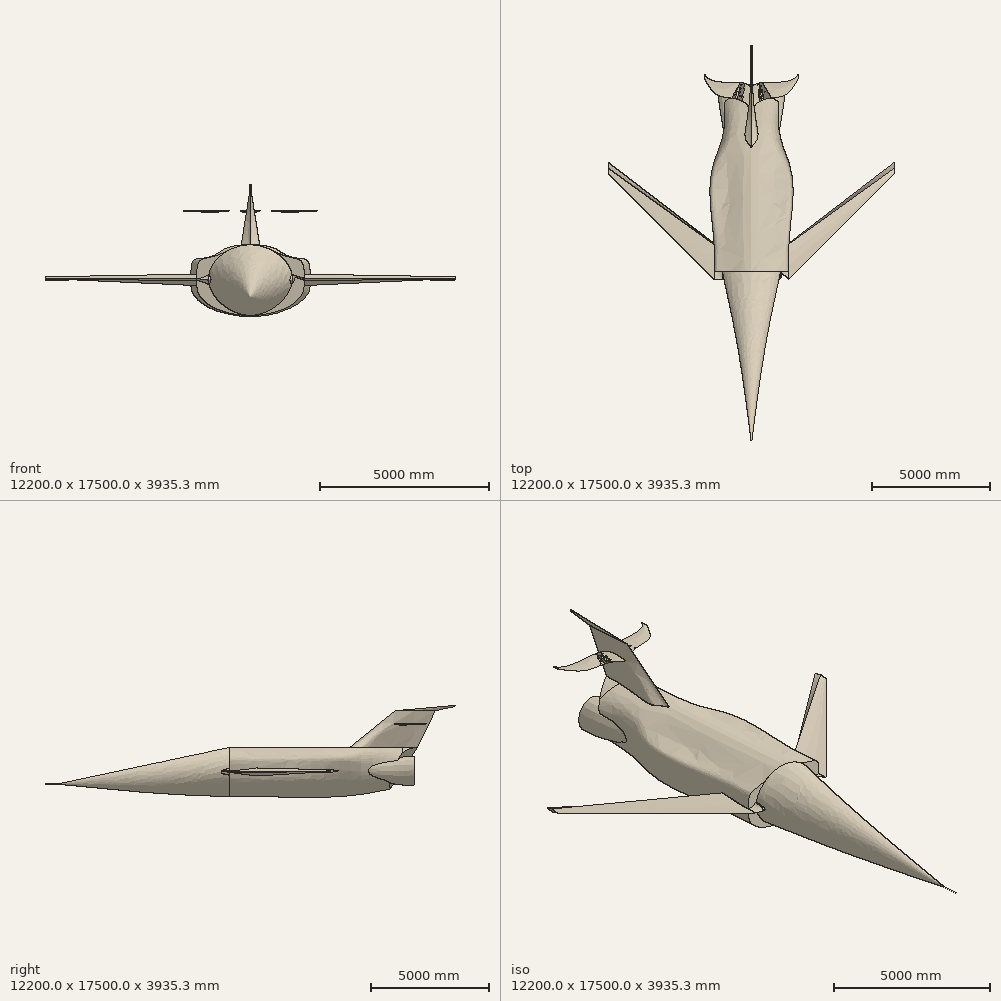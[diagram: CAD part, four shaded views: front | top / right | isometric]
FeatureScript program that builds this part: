
annotation { "Feature Type Name" : "Feature", "Feature Type Description" : "" }
export const myFeature = defineFeature(function(context is Context, id is Id, definition is map)
    precondition{}
    {
        {
            var Q0;
            Q0=qCreatedBy(makeId("Right.planeOp"),FACE);
            var sketch = newSketch(context, id + "F0", { "sketchPlane" : qUnion([Q0])});
            skLineSegment(sketch, "E0", {"start": v(0, 0) * mm, "end": v(-1750, 0) * mm});
            skLineSegment(sketch, "E1", {"start": v(-1750, 0) * mm, "end": v(-3500, 0) * mm});
            skLineSegment(sketch, "E2", {"start": v(-3500, 0) * mm, "end": v(-3500, -1000) * mm});
            skLineSegment(sketch, "E3", {"start": v(-3500, -1000) * mm, "end": v(-8500, -1000) * mm});
            skLineSegment(sketch, "E4", {"start": v(-8500, -1000) * mm, "end": v(-8500, -562.6) * mm});
            skLineSegment(sketch, "E5", {"start": v(-1164.59, 0) * mm, "end": v(-1164.59, 1000) * mm});
            skLineSegment(sketch, "E6", {"start": v(-1164.59, 1000) * mm, "end": v(-8500, -562.6) * mm});
            skLineSegment(sketch, "E7", {"start": v(-8500, -562.6) * mm, "end": v(-3500, -1000) * mm});
            skLineSegment(sketch, "E8", {"start": v(-3500, 0) * mm, "end": v(-3500, 502.5) * mm});
            skLineSegment(sketch, "E9", {"start": v(-8500, -562.6) * mm, "end": v(-8450, -562.6) * mm});
            skLineSegment(sketch, "E10", {"start": v(-8450, -562.6) * mm, "end": v(-8450, -551.95) * mm});
            skLineSegment(sketch, "E11", {"start": v(-8450, -562.6) * mm, "end": v(-8450, -566.97) * mm});
            skSolve(sketch);
        }
        {
            var Q0;
            Q0=sQuery(id+"F0.wireOp",EDGE,"E5");
            cPlane(context, id + "F1", {"entities" : qUnion([Q0]), "cplaneType" : CPlaneType.LINE_ANGLE, "offset" : 25 * mm, "angle" : 90 * degree, "oppositeDirection" : true, "width" : 150 * mm, "height" : 150 * mm});
        }
        {
            var Q0;
            Q0=qCreatedBy(id+"F1.planeOp",FACE);
            var sketch = newSketch(context, id + "F2", { "sketchPlane" : qUnion([Q0])});
            skPoint(sketch, "E12.middle", {"position": v(0, 0) * mm});
            skFitSpline(sketch, "E13", {"points": [v(0, 1000) * mm, v(-1060, 662.5) * mm, v(-1517.6, 506.84) * mm, v(-1600, 0) * mm, v(-1517.6, -506.84) * mm, v(-750, -1000) * mm, v(750, -1000) * mm, v(1517.6, -506.84) * mm, v(1600, 0) * mm, v(1517.6, 506.84) * mm, v(1060, 662.5) * mm, v(0, 1000) * mm]});
            skSolve(sketch);
        }
        {
            var Q0;
            Q0=qCreatedBy(makeId("Front.planeOp"),FACE);
            var sketch = newSketch(context, id + "F3", { "sketchPlane" : qUnion([Q0])});
            skPoint(sketch, "E14.middle", {"position": v(0, 0) * mm});
            skFitSpline(sketch, "E15", {"points": [v(0, 1000) * mm, v(-1060, 662.5) * mm, v(-1517.6, 506.84) * mm, v(-1600, 0) * mm, v(-1517.6, -506.84) * mm, v(-750, -1000) * mm, v(750, -1000) * mm, v(1517.6, -506.84) * mm, v(1600, 0) * mm, v(1517.6, 506.84) * mm, v(1060, 662.5) * mm, v(0, 1000) * mm]});
            skSolve(sketch);
        }
        {
            var Q0;
            Q0=qCreatedBy(makeId("Front.planeOp"),FACE);
            cPlane(context, id + "F4", {"entities" : qUnion([Q0]), "cplaneType" : CPlaneType.OFFSET, "offset" : 3500 * mm, "oppositeDirection" : true, "width" : 150 * mm, "height" : 150 * mm});
        }
        {
            var Q0;
            Q0=qCreatedBy(id+"F4.planeOp",FACE);
            var sketch = newSketch(context, id + "F5", { "sketchPlane" : qUnion([Q0])});
            skPoint(sketch, "E16.middle", {"position": v(0, 0) * mm});
            skFitSpline(sketch, "E17", {"points": [v(0, 1000) * mm, v(-1060, 662.5) * mm, v(-1517.6, 506.84) * mm, v(-1600, 0) * mm, v(-1517.6, -506.84) * mm, v(-750, -1000) * mm, v(750, -1000) * mm, v(1517.6, -506.84) * mm, v(1600, 0) * mm, v(1517.6, 506.84) * mm, v(1060, 662.5) * mm, v(0, 1000) * mm]});
            skSolve(sketch);
        }
        {
            var Q0;
            Q0=qCreatedBy(makeId("Front.planeOp"),FACE);
            cPlane(context, id + "F6", {"entities" : qUnion([Q0]), "cplaneType" : CPlaneType.OFFSET, "offset" : 4500 * mm, "oppositeDirection" : true, "width" : 150 * mm, "height" : 150 * mm});
        }
        {
            var Q0;
            Q0=qCreatedBy(id+"F6.planeOp",FACE);
            var sketch = newSketch(context, id + "F7", { "sketchPlane" : qUnion([Q0])});
            skPoint(sketch, "E18.middle", {"position": v(0, 0) * mm});
            skFitSpline(sketch, "E19", {"points": [v(0, 1000) * mm, v(-1060, 662.5) * mm, v(-1250, 0) * mm, v(-1060, -662.5) * mm, v(0, -1000) * mm, v(1060, -662.5) * mm, v(1250, 0) * mm, v(1060, 662.5) * mm, v(0, 1000) * mm]});
            skSolve(sketch);
        }
        {
            var Q0;
            Q0=qCreatedBy(makeId("Front.planeOp"),FACE);
            cPlane(context, id + "F8", {"entities" : qUnion([Q0]), "cplaneType" : CPlaneType.OFFSET, "offset" : 6232.05 * mm, "oppositeDirection" : true, "width" : 150 * mm, "height" : 150 * mm});
        }
        {
            var Q0;
            Q0=qCreatedBy(id+"F8.planeOp",FACE);
            var sketch = newSketch(context, id + "F9", { "sketchPlane" : qUnion([Q0])});
            skPoint(sketch, "E20.middle", {"position": v(0, 0) * mm});
            skFitSpline(sketch, "E21", {"points": [v(0, 1000) * mm, v(-1060, 662.5) * mm, v(-1250, 0) * mm, v(-848, -530) * mm, v(848, -530) * mm, v(1250, 0) * mm, v(1060, 662.5) * mm, v(0, 1000) * mm]});
            skSolve(sketch);
        }
        {
            var Q0;
            Q0=makeQuery(id+"F2.imprint","IMPRINT",FACE,{"disambiguationData":[TD([[makeQuery(id+"F2.imprint","IMPRINT",EDGE,{"derivedFrom":sQuery(id+"F2.wireOp",EDGE,"E13")}),1.0]])]});
            var Q1;
            Q1=makeQuery(id+"F3.imprint","IMPRINT",FACE,{"disambiguationData":[TD([[makeQuery(id+"F3.imprint","IMPRINT",EDGE,{"derivedFrom":sQuery(id+"F3.wireOp",EDGE,"E15")}),1.0]])]});
            var Q2;
            Q2=makeQuery(id+"F5.imprint","IMPRINT",FACE,{"disambiguationData":[TD([[makeQuery(id+"F5.imprint","IMPRINT",EDGE,{"derivedFrom":sQuery(id+"F5.wireOp",EDGE,"E17")}),1.0]])]});
            var Q3;
            Q3=makeQuery(id+"F7.imprint","IMPRINT",FACE,{"disambiguationData":[TD([[makeQuery(id+"F7.imprint","IMPRINT",EDGE,{"derivedFrom":sQuery(id+"F7.wireOp",EDGE,"E19")}),1.0]])]});
            var Q4;
            Q4=makeQuery(id+"F9.imprint","IMPRINT",FACE,{"disambiguationData":[TD([[makeQuery(id+"F9.imprint","IMPRINT",EDGE,{"derivedFrom":sQuery(id+"F9.wireOp",EDGE,"E21")}),1.0]])]});
            loft(context, id + "F10", {"sheetProfilesArray" : [{ "sheetProfileEntities" : qUnion([Q0]) }, { "sheetProfileEntities" : qUnion([Q1]) }, { "sheetProfileEntities" : qUnion([Q2]) }, { "sheetProfileEntities" : qUnion([Q3]) }, { "sheetProfileEntities" : qUnion([Q4]) }]});
        }
        {
            var Q0;
            Q0=makeQuery(id+"F10.opLoft","CAP_FACE",FACE,{"disambiguationData":[OSD([makeQuery(id+"F9.imprint","IMPRINT",FACE,{"disambiguationData":[TD([[makeQuery(id+"F9.imprint","IMPRINT",EDGE,{"derivedFrom":sQuery(id+"F9.wireOp",EDGE,"E21")}),1.0]])]})])],"isStart":true});
            extrude(context, id + "F11", {"entities" : qUnion([Q0]), "operationType" : NewBodyOperationType.ADD, "depth" : 649.4 * mm, "offsetDistance" : 25 * mm});
        }
        {
            var Q0;
            Q0=qCreatedBy(makeId("Right.planeOp"),FACE);
            var sketch = newSketch(context, id + "F12", { "sketchPlane" : qUnion([Q0])});
            skLineSegment(sketch, "E22", {"start": v(0, 0) * mm, "end": v(4500, 0) * mm});
            skLineSegment(sketch, "E23", {"start": v(4500, 0) * mm, "end": v(6232.05, 0) * mm});
            skLineSegment(sketch, "E24", {"start": v(4500, 0) * mm, "end": v(4500, 1000) * mm});
            skLineSegment(sketch, "E25", {"start": v(4500, 1000) * mm, "end": v(6881.46, 1000) * mm});
            skLineSegment(sketch, "E26", {"start": v(6881.46, 1000) * mm, "end": v(6881.46, -1000) * mm});
            skLineSegment(sketch, "E27", {"start": v(6881.46, 1000) * mm, "end": v(6232.05, 0) * mm});
            skLineSegment(sketch, "E28", {"start": v(6232.05, 0) * mm, "end": v(5582.64, -1000) * mm});
            skLineSegment(sketch, "E29", {"start": v(5582.64, -1000) * mm, "end": v(6881.46, -1000) * mm});
            skSolve(sketch);
        }
        {
            var Q0;
            Q0=makeQuery(id+"F12.imprint","IMPRINT",FACE,{"disambiguationData":[TD([[makeQuery(id+"F12.imprint","IMPRINT",EDGE,{"derivedFrom":sQuery(id+"F12.wireOp",EDGE,"E26")}),-1.0]])]});
            var Q1;
            Q1=sQuery(id+"F12.wireOp",EDGE,"E25");
            revolve(context, id + "F13", {"operationType" : NewBodyOperationType.REMOVE, "entities" : qUnion([Q0]), "axis" : qUnion([Q1]), "revolveType" : RevolveType.SYMMETRIC, "oppositeDirection" : true, "angle" : 182 * degree});
        }
        {
            var Q0;
            Q0=qCreatedBy(id+"F1.planeOp",FACE);
            var sketch = newSketch(context, id + "F14", { "sketchPlane" : qUnion([Q0])});
            skFitSpline(sketch, "E30", {"points": [v(0, 1000) * mm, v(-1250, 0) * mm, v(0, -1099.92) * mm, v(1250, 0) * mm, v(0, 1000) * mm]});
            skSolve(sketch);
        }
        {
            var Q0;
            Q0=qCreatedBy(makeId("Front.planeOp"),FACE);
            cPlane(context, id + "F15", {"entities" : qUnion([Q0]), "cplaneType" : CPlaneType.OFFSET, "offset" : 3500 * mm, "width" : 150 * mm, "height" : 150 * mm});
        }
        {
            var Q0;
            Q0=qCreatedBy(id+"F15.planeOp",FACE);
            var sketch = newSketch(context, id + "F16", { "sketchPlane" : qUnion([Q0])});
            skCircle(sketch, "E31", {"center": v(0, -248.75) * mm, "radius": 751.25 * mm});
            skSolve(sketch);
        }
        {
            var Q0;
            Q0=qCreatedBy(makeId("Front.planeOp"),FACE);
            cPlane(context, id + "F17", {"entities" : qUnion([Q0]), "cplaneType" : CPlaneType.OFFSET, "offset" : 8450 * mm, "width" : 150 * mm, "height" : 150 * mm});
        }
        {
            var Q0;
            Q0=qCreatedBy(id+"F17.planeOp",FACE);
            var sketch = newSketch(context, id + "F18", { "sketchPlane" : qUnion([Q0])});
            skCircle(sketch, "E32", {"center": v(0, -559.46) * mm, "radius": 7.51 * mm});
            skSolve(sketch);
        }
        {
            var Q1;
            Q1=makeQuery(id+"F18.imprint","IMPRINT",FACE,{"disambiguationData":[TD([[makeQuery(id+"F18.imprint","IMPRINT",EDGE,{"derivedFrom":sQuery(id+"F18.wireOp",EDGE,"E32")}),1.0]])]});
            var Q2;
            Q2=makeQuery(id+"F16.imprint","IMPRINT",FACE,{"disambiguationData":[TD([[makeQuery(id+"F16.imprint","IMPRINT",EDGE,{"derivedFrom":sQuery(id+"F16.wireOp",EDGE,"E31")}),1.0]])]});
            var Q3;
            Q3=makeQuery(id+"F14.imprint","IMPRINT",FACE,{"disambiguationData":[TD([[makeQuery(id+"F14.imprint","IMPRINT",EDGE,{"derivedFrom":sQuery(id+"F14.wireOp",EDGE,"E30")}),1.0]])]});
            loft(context, id + "F19", {"operationType" : NewBodyOperationType.ADD, "sheetProfilesArray" : [{ "sheetProfileEntities" : qUnion([Q1]) }, { "sheetProfileEntities" : qUnion([Q2]) }, { "sheetProfileEntities" : qUnion([Q3]) }]});
        }
        {
            var Q0;
            Q0=makeQuery(id+"F19.opLoft","CAP_FACE",FACE,{"disambiguationData":[OSD([makeQuery(id+"F18.imprint","IMPRINT",FACE,{"disambiguationData":[TD([[makeQuery(id+"F18.imprint","IMPRINT",EDGE,{"derivedFrom":sQuery(id+"F18.wireOp",EDGE,"E32")}),1.0]])]})])],"isStart":true});
            extrude(context, id + "F20", {"entities" : qUnion([Q0]), "operationType" : NewBodyOperationType.ADD, "depth" : 550 * mm, "offsetDistance" : 25 * mm});
        }
        {
            var Q0;
            Q0=qCreatedBy(makeId("Front.planeOp"),FACE);
            cPlane(context, id + "F21", {"entities" : qUnion([Q0]), "cplaneType" : CPlaneType.OFFSET, "offset" : 3500 * mm, "oppositeDirection" : true, "width" : 150 * mm, "height" : 150 * mm});
        }
        {
            var Q0;
            Q0=qCreatedBy(id+"F21.planeOp",FACE);
            var sketch = newSketch(context, id + "F22", { "sketchPlane" : qUnion([Q0])});
            skCircle(sketch, "E33", {"center": v(-800, 0) * mm, "radius": 600 * mm});
            skCircle(sketch, "E34", {"center": v(800, 0) * mm, "radius": 600 * mm});
            skSolve(sketch);
        }
        {
            var Q0;
            Q0=qCreatedBy(makeId("Front.planeOp"),FACE);
            cPlane(context, id + "F23", {"entities" : qUnion([Q0]), "cplaneType" : CPlaneType.OFFSET, "offset" : 4500 * mm, "oppositeDirection" : true, "width" : 150 * mm, "height" : 150 * mm});
        }
        {
            var Q0;
            Q0=qCreatedBy(id+"F23.planeOp",FACE);
            var sketch = newSketch(context, id + "F24", { "sketchPlane" : qUnion([Q0])});
            skCircle(sketch, "E35", {"center": v(-800, 0) * mm, "radius": 400 * mm});
            skCircle(sketch, "E36", {"center": v(800, 0) * mm, "radius": 400 * mm});
            skSolve(sketch);
        }
        {
            var Q0;
            Q0=qCreatedBy(makeId("Front.planeOp"),FACE);
            cPlane(context, id + "F25", {"entities" : qUnion([Q0]), "cplaneType" : CPlaneType.OFFSET, "offset" : 6232.05 * mm, "oppositeDirection" : true, "width" : 150 * mm, "height" : 150 * mm});
        }
        {
            var Q0;
            Q0=qCreatedBy(id+"F25.planeOp",FACE);
            var sketch = newSketch(context, id + "F26", { "sketchPlane" : qUnion([Q0])});
            skCircle(sketch, "E37", {"center": v(-800, 0) * mm, "radius": 600 * mm});
            skCircle(sketch, "E38", {"center": v(800, 0) * mm, "radius": 600 * mm});
            skSolve(sketch);
        }
        {
            var Q0;
            Q0=qCreatedBy(makeId("Front.planeOp"),FACE);
            cPlane(context, id + "F27", {"entities" : qUnion([Q0]), "cplaneType" : CPlaneType.OFFSET, "offset" : 6732.05 * mm, "oppositeDirection" : true, "width" : 150 * mm, "height" : 150 * mm});
        }
        {
            var Q0;
            Q0=qCreatedBy(id+"F27.planeOp",FACE);
            var sketch = newSketch(context, id + "F28", { "sketchPlane" : qUnion([Q0])});
            skCircle(sketch, "E39", {"center": v(-800, 0) * mm, "radius": 600 * mm});
            skCircle(sketch, "E40", {"center": v(800, 0) * mm, "radius": 600 * mm});
            skSolve(sketch);
        }
        {
            var Q0;
            Q0=makeQuery(id+"F22.imprint","IMPRINT",FACE,{"disambiguationData":[TD([[makeQuery(id+"F22.imprint","IMPRINT",EDGE,{"derivedFrom":sQuery(id+"F22.wireOp",EDGE,"E33")}),1.0]])]});
            var Q1;
            Q1=makeQuery(id+"F24.imprint","IMPRINT",FACE,{"disambiguationData":[TD([[makeQuery(id+"F24.imprint","IMPRINT",EDGE,{"derivedFrom":sQuery(id+"F24.wireOp",EDGE,"E35")}),1.0]])]});
            var Q2;
            Q2=makeQuery(id+"F26.imprint","IMPRINT",FACE,{"disambiguationData":[TD([[makeQuery(id+"F26.imprint","IMPRINT",EDGE,{"derivedFrom":sQuery(id+"F26.wireOp",EDGE,"E37")}),1.0]])]});
            var Q3;
            Q3=makeQuery(id+"F28.imprint","IMPRINT",FACE,{"disambiguationData":[TD([[makeQuery(id+"F28.imprint","IMPRINT",EDGE,{"derivedFrom":sQuery(id+"F28.wireOp",EDGE,"E39")}),1.0]])]});
            loft(context, id + "F29", {"sheetProfilesArray" : [{ "sheetProfileEntities" : qUnion([Q0]) }, { "sheetProfileEntities" : qUnion([Q1]) }, { "sheetProfileEntities" : qUnion([Q2]) }, { "sheetProfileEntities" : qUnion([Q3]) }]});
        }
        {
            var Q0;
            Q0=makeQuery(id+"F22.imprint","IMPRINT",FACE,{"disambiguationData":[TD([[makeQuery(id+"F22.imprint","IMPRINT",EDGE,{"derivedFrom":sQuery(id+"F22.wireOp",EDGE,"E34")}),1.0]])]});
            var Q1;
            Q1=makeQuery(id+"F24.imprint","IMPRINT",FACE,{"disambiguationData":[TD([[makeQuery(id+"F24.imprint","IMPRINT",EDGE,{"derivedFrom":sQuery(id+"F24.wireOp",EDGE,"E36")}),1.0]])]});
            var Q2;
            Q2=makeQuery(id+"F26.imprint","IMPRINT",FACE,{"disambiguationData":[TD([[makeQuery(id+"F26.imprint","IMPRINT",EDGE,{"derivedFrom":sQuery(id+"F26.wireOp",EDGE,"E38")}),1.0]])]});
            var Q3;
            Q3=makeQuery(id+"F28.imprint","IMPRINT",FACE,{"disambiguationData":[TD([[makeQuery(id+"F28.imprint","IMPRINT",EDGE,{"derivedFrom":sQuery(id+"F28.wireOp",EDGE,"E40")}),1.0]])]});
            loft(context, id + "F30", {"sheetProfilesArray" : [{ "sheetProfileEntities" : qUnion([Q0]) }, { "sheetProfileEntities" : qUnion([Q1]) }, { "sheetProfileEntities" : qUnion([Q2]) }, { "sheetProfileEntities" : qUnion([Q3]) }]});
        }
        {
            var Q0;
            Q0=qCreatedBy(makeId("Right.planeOp"),FACE);
            var sketch = newSketch(context, id + "F31", { "sketchPlane" : qUnion([Q0])});
            skFitSpline(sketch, "E41", {"points": [v(-1500, -50) * mm, v(0, 250) * mm, v(3000, -50) * mm, v(0, -250) * mm, v(-1500, -50) * mm]});
            skSolve(sketch);
        }
        {
            var Q0;
            Q0=qCreatedBy(makeId("Right.planeOp"),FACE);
            cPlane(context, id + "F32", {"entities" : qUnion([Q0]), "cplaneType" : CPlaneType.OFFSET, "offset" : 1600 * mm, "oppositeDirection" : true, "width" : 150 * mm, "height" : 150 * mm});
        }
        {
            var Q0;
            Q0=qCreatedBy(id+"F32.planeOp",FACE);
            var sketch = newSketch(context, id + "F33", { "sketchPlane" : qUnion([Q0])});
            skFitSpline(sketch, "E42", {"points": [v(-1500, 0) * mm, v(1000, 250) * mm, v(3500, 0) * mm], "startDerivative": vector(7500, 0) * mm, "endDerivative": vector(7500, 0) * mm});
            skFitSpline(sketch, "E43", {"points": [v(-1500, 0) * mm, v(1000, -250) * mm, v(3500, 0) * mm], "startDerivative": vector(5000, -750) * mm, "endDerivative": vector(7500, 0) * mm});
            skSolve(sketch);
        }
        {
            var Q0;
            Q0=qCreatedBy(makeId("Right.planeOp"),FACE);
            cPlane(context, id + "F34", {"entities" : qUnion([Q0]), "cplaneType" : CPlaneType.OFFSET, "offset" : 1600 * mm, "width" : 150 * mm, "height" : 150 * mm});
        }
        {
            var Q0;
            Q0=qCreatedBy(id+"F34.planeOp",FACE);
            var sketch = newSketch(context, id + "F35", { "sketchPlane" : qUnion([Q0])});
            skFitSpline(sketch, "E44", {"points": [v(-1500, 0) * mm, v(1000, 250) * mm, v(3500, 0) * mm], "startDerivative": vector(7500, 0) * mm, "endDerivative": vector(7500, 0) * mm});
            skFitSpline(sketch, "E45", {"points": [v(-1500, 0) * mm, v(1000, -250) * mm, v(3500, 0) * mm], "startDerivative": vector(5000, -750) * mm, "endDerivative": vector(7500, 0) * mm});
            skSolve(sketch);
        }
        {
            var Q0;
            Q0=qCreatedBy(makeId("Right.planeOp"),FACE);
            cPlane(context, id + "F36", {"entities" : qUnion([Q0]), "cplaneType" : CPlaneType.OFFSET, "offset" : 6100 * mm, "oppositeDirection" : true, "width" : 150 * mm, "height" : 150 * mm});
        }
        {
            var Q0;
            Q0=qCreatedBy(id+"F36.planeOp",FACE);
            var sketch = newSketch(context, id + "F37", { "sketchPlane" : qUnion([Q0])});
            skFitSpline(sketch, "E46", {"points": [v(3000, 0) * mm, v(3250, 50) * mm, v(3500, 0) * mm], "startDerivative": vector(750, 0) * mm, "endDerivative": vector(750, 0) * mm});
            skFitSpline(sketch, "E47", {"points": [v(3000, 0) * mm, v(3250, -50) * mm, v(3500, 0) * mm], "startDerivative": vector(500, -150) * mm, "endDerivative": vector(750, 0) * mm});
            skSolve(sketch);
        }
        {
            var Q0;
            Q0=qCreatedBy(makeId("Right.planeOp"),FACE);
            cPlane(context, id + "F38", {"entities" : qUnion([Q0]), "cplaneType" : CPlaneType.OFFSET, "offset" : 6100 * mm, "width" : 150 * mm, "height" : 150 * mm});
        }
        {
            var Q0;
            Q0=qCreatedBy(id+"F38.planeOp",FACE);
            var sketch = newSketch(context, id + "F39", { "sketchPlane" : qUnion([Q0])});
            skFitSpline(sketch, "E48", {"points": [v(3000, 0) * mm, v(3250, 50) * mm, v(3500, 0) * mm], "startDerivative": vector(750, 0) * mm, "endDerivative": vector(750, 0) * mm});
            skFitSpline(sketch, "E49", {"points": [v(3000, 0) * mm, v(3250, -50) * mm, v(3500, 0) * mm], "startDerivative": vector(500, -150) * mm, "endDerivative": vector(750, 0) * mm});
            skSolve(sketch);
        }
        {
            var Q0;
            Q0=qSketchRegion(id+"F31",true);
            extrude(context, id + "F40", {"entities" : qUnion([Q0]), "endBound" : BoundingType.SYMMETRIC, "depth" : 2500 * mm, "offsetDistance" : 25 * mm});
        }
        {
            var Q1;
            Q1=makeQuery(id+"F40.opExtrude","CAP_FACE",FACE,{"disambiguationData":[OSD([sQuery(id+"F31.wireOp",EDGE,"E41")])],"isStart":true});
            var Q2;
            {var subQ0=sQuery(id+"F33.wireOp",EDGE,"E42");Q2=makeQuery(id+"F33.imprint","IMPRINT",FACE,{"disambiguationData":[TD([[makeQuery(id+"F33.imprint","IMPRINT",EDGE,{"derivedFrom":subQ0}),-1.0]])]});}
            loft(context, id + "F41", {"operationType" : NewBodyOperationType.ADD, "sheetProfilesArray" : [{ "sheetProfileEntities" : qUnion([Q1]) }, { "sheetProfileEntities" : qUnion([Q2]) }]});
        }
        {
            var Q1;
            Q1=makeQuery(id+"F40.opExtrude","CAP_FACE",FACE,{"disambiguationData":[OSD([sQuery(id+"F31.wireOp",EDGE,"E41")])],"isStart":false});
            var Q2;
            {var subQ0=sQuery(id+"F35.wireOp",EDGE,"E44");Q2=makeQuery(id+"F35.imprint","IMPRINT",FACE,{"disambiguationData":[TD([[makeQuery(id+"F35.imprint","IMPRINT",EDGE,{"derivedFrom":subQ0}),-1.0]])]});}
            loft(context, id + "F42", {"operationType" : NewBodyOperationType.ADD, "sheetProfilesArray" : [{ "sheetProfileEntities" : qUnion([Q1]) }, { "sheetProfileEntities" : qUnion([Q2]) }]});
        }
        {
            var Q1;
            {var subQ0=sQuery(id+"F33.wireOp",EDGE,"E42");Q1=makeQuery(id+"F41.opLoft","CAP_FACE",FACE,{"disambiguationData":[OSD([makeQuery(id+"F33.imprint","IMPRINT",FACE,{"disambiguationData":[TD([[makeQuery(id+"F33.imprint","IMPRINT",EDGE,{"derivedFrom":subQ0}),-1.0]])]})])],"isStart":true});}
            var Q2;
            {var subQ0=sQuery(id+"F37.wireOp",EDGE,"E46");Q2=makeQuery(id+"F37.imprint","IMPRINT",FACE,{"disambiguationData":[TD([[makeQuery(id+"F37.imprint","IMPRINT",EDGE,{"derivedFrom":subQ0}),-1.0]])]});}
            loft(context, id + "F43", {"operationType" : NewBodyOperationType.ADD, "sheetProfilesArray" : [{ "sheetProfileEntities" : qUnion([Q1]) }, { "sheetProfileEntities" : qUnion([Q2]) }]});
        }
        {
            var Q1;
            {var subQ0=sQuery(id+"F35.wireOp",EDGE,"E44");Q1=makeQuery(id+"F42.opLoft","CAP_FACE",FACE,{"disambiguationData":[OSD([makeQuery(id+"F35.imprint","IMPRINT",FACE,{"disambiguationData":[TD([[makeQuery(id+"F35.imprint","IMPRINT",EDGE,{"derivedFrom":subQ0}),-1.0]])]})])],"isStart":true});}
            var Q2;
            {var subQ0=sQuery(id+"F39.wireOp",EDGE,"E48");Q2=makeQuery(id+"F39.imprint","IMPRINT",FACE,{"disambiguationData":[TD([[makeQuery(id+"F39.imprint","IMPRINT",EDGE,{"derivedFrom":subQ0}),-1.0]])]});}
            loft(context, id + "F44", {"operationType" : NewBodyOperationType.ADD, "sheetProfilesArray" : [{ "sheetProfileEntities" : qUnion([Q1]) }, { "sheetProfileEntities" : qUnion([Q2]) }]});
        }
        {
            var Q0;
            Q0=qCreatedBy(makeId("Right.planeOp"),FACE);
            var sketch = newSketch(context, id + "F45", { "sketchPlane" : qUnion([Q0])});
            skLineSegment(sketch, "E50", {"start": v(0, 0) * mm, "end": v(4500, 0) * mm});
            skLineSegment(sketch, "E51", {"start": v(4500, 0) * mm, "end": v(4500, 1000) * mm});
            skLineSegment(sketch, "E52", {"start": v(4500, 1000) * mm, "end": v(4500, 750) * mm});
            skLineSegment(sketch, "E53", {"start": v(4500, 750) * mm, "end": v(4000, 750) * mm});
            skLineSegment(sketch, "E54", {"start": v(4500, 750) * mm, "end": v(6250, 750) * mm});
            skLineSegment(sketch, "E55", {"start": v(4500, 1000) * mm, "end": v(4000, 1000) * mm});
            skLineSegment(sketch, "E56", {"start": v(4500, 1000) * mm, "end": v(6881.46, 1000) * mm});
            skLineSegment(sketch, "E57", {"start": v(6881.46, 1000) * mm, "end": v(8500, 1000) * mm});
            skLineSegment(sketch, "E58", {"start": v(8500, 1000) * mm, "end": v(8500, 2800) * mm});
            skLineSegment(sketch, "E59", {"start": v(6881.46, 1000) * mm, "end": v(7648.6, 2572.89) * mm});
            skLineSegment(sketch, "E60", {"start": v(7648.6, 2572.89) * mm, "end": v(5943.2, 2572.89) * mm});
            skLineSegment(sketch, "E61", {"start": v(5943.2, 2572.89) * mm, "end": v(4000, 1000) * mm});
            skSolve(sketch);
        }
        {
            var Q0;
            Q0=qCreatedBy(makeId("Top.planeOp"),FACE);
            cPlane(context, id + "F46", {"entities" : qUnion([Q0]), "cplaneType" : CPlaneType.OFFSET, "offset" : 750 * mm, "width" : 150 * mm, "height" : 150 * mm});
        }
        {
            var Q0;
            Q0=qCreatedBy(id+"F46.planeOp",FACE);
            var sketch = newSketch(context, id + "F47", { "sketchPlane" : qUnion([Q0])});
            skFitSpline(sketch, "E62", {"points": [v(0, 4000) * mm, v(-250, 4500) * mm, v(0, 6250) * mm], "startDerivative": vector(-889.86, 1147.1) * mm, "endDerivative": vector(737.87, 3164.53) * mm});
            skFitSpline(sketch, "E63", {"points": [v(0, 4000) * mm, v(250, 4500) * mm, v(0, 6250) * mm], "startDerivative": vector(889.86, 1147.1) * mm, "endDerivative": vector(-737.87, 3164.53) * mm});
            skSolve(sketch);
        }
        {
            var Q0;
            Q0=qCreatedBy(makeId("Top.planeOp"),FACE);
            cPlane(context, id + "F48", {"entities" : qUnion([Q0]), "cplaneType" : CPlaneType.OFFSET, "offset" : 1000 * mm, "width" : 150 * mm, "height" : 150 * mm});
        }
        {
            var Q0;
            Q0=qCreatedBy(id+"F48.planeOp",FACE);
            var sketch = newSketch(context, id + "F49", { "sketchPlane" : qUnion([Q0])});
            skFitSpline(sketch, "E64", {"points": [v(0, 4000) * mm, v(-250, 4500) * mm, v(0, 6881.46) * mm], "startDerivative": vector(0, 2302.24) * mm, "endDerivative": vector(0, 5298.17) * mm});
            skFitSpline(sketch, "E65", {"points": [v(0, 4000) * mm, v(250, 4500) * mm, v(0, 6881.46) * mm], "startDerivative": vector(0, 2302.24) * mm, "endDerivative": vector(0, 5298.17) * mm});
            skSolve(sketch);
        }
        {
            var Q0;
            Q0=sQuery(id+"F45.wireOp",EDGE,"E60");
            cPlane(context, id + "F50", {"entities" : qUnion([Q0]), "cplaneType" : CPlaneType.LINE_ANGLE, "offset" : 25 * mm, "angle" : 180 * degree, "width" : 150 * mm, "height" : 150 * mm});
        }
        {
            var Q0;
            Q0=qCreatedBy(id+"F50.planeOp",FACE);
            var sketch = newSketch(context, id + "F51", { "sketchPlane" : qUnion([Q0])});
            skFitSpline(sketch, "E66", {"points": [v(0, 5943.2) * mm, v(-25, 6795.9) * mm, v(0, 7648.6) * mm], "startDerivative": vector(-75, 1705.4) * mm, "endDerivative": vector(75, 1705.4) * mm});
            skFitSpline(sketch, "E67", {"points": [v(0, 5943.2) * mm, v(25, 6795.9) * mm, v(0, 7648.6) * mm], "startDerivative": vector(75, 1705.4) * mm, "endDerivative": vector(-75, 1705.4) * mm});
            skSolve(sketch);
        }
        {
            var Q0;
            Q0=qCreatedBy(makeId("Front.planeOp"),FACE);
            cPlane(context, id + "F52", {"entities" : qUnion([Q0]), "cplaneType" : CPlaneType.OFFSET, "offset" : 8500 * mm, "oppositeDirection" : true, "width" : 150 * mm, "height" : 150 * mm});
        }
        {
            var Q0;
            Q0=qCreatedBy(id+"F52.planeOp",FACE);
            var sketch = newSketch(context, id + "F53", { "sketchPlane" : qUnion([Q0])});
            skCircle(sketch, "E68", {"center": v(0, 2775) * mm, "radius": 25 * mm});
            skSolve(sketch);
        }
        {
            var Q0;
            Q0=qCreatedBy(makeId("Right.planeOp"),FACE);
            var sketch = newSketch(context, id + "F54", { "sketchPlane" : qUnion([Q0])});
            skLineSegment(sketch, "E69", {"start": v(5943.2, 2572.89) * mm, "end": v(8500, 2800) * mm});
            skSolve(sketch);
        }
        {
            var Q1;
            Q1 = qSketchRegion(id + "F47", true);
            var Q2;
            Q2 = qSketchRegion(id + "F49", true);
            loft(context, id + "F55", {"sheetProfilesArray" : [{ "sheetProfileEntities" : qUnion([Q1]) }, { "sheetProfileEntities" : qUnion([Q2]) }]});
        }
        {
            var Q1;
            {var subQ0=sQuery(id+"F49.wireOp",EDGE,"E64");Q1=makeQuery(id+"F55.opLoft","CAP_FACE",FACE,{"disambiguationData":[OSD([makeQuery(id+"F49.imprint","IMPRINT",FACE,{"disambiguationData":[TD([[makeQuery(id+"F49.imprint","IMPRINT",EDGE,{"derivedFrom":subQ0}),-1.0]])]})])],"isStart":true});}
            var Q2;
            Q2=makeQuery(id+"F51.imprint","IMPRINT",FACE,{"disambiguationData":[TD([[makeQuery(id+"F51.imprint","IMPRINT",EDGE,{"derivedFrom":sQuery(id+"F51.wireOp",EDGE,"E66")}),-1.0]])]});
            loft(context, id + "F56", {"operationType" : NewBodyOperationType.ADD, "sheetProfilesArray" : [{ "sheetProfileEntities" : qUnion([Q1]) }, { "sheetProfileEntities" : qUnion([Q2]) }]});
        }
        {
            var Q1;
            Q1=makeQuery(id+"F56.opLoft","CAP_FACE",FACE,{"disambiguationData":[OSD([makeQuery(id+"F51.imprint","IMPRINT",FACE,{"disambiguationData":[TD([[makeQuery(id+"F51.imprint","IMPRINT",EDGE,{"derivedFrom":sQuery(id+"F51.wireOp",EDGE,"E66")}),-1.0]])]})])],"isStart":true});
            var Q2;
            Q2=makeQuery(id+"F53.imprint","IMPRINT",FACE,{"disambiguationData":[TD([[makeQuery(id+"F53.imprint","IMPRINT",EDGE,{"derivedFrom":sQuery(id+"F53.wireOp",EDGE,"E68")}),1.0]])]});
            var Q3;
            Q3=sQuery(id+"F54.wireOp",EDGE,"E69");
            loft(context, id + "F57", {"operationType" : NewBodyOperationType.ADD, "addGuides" : true, "sheetProfilesArray" : [{ "sheetProfileEntities" : qUnion([Q1]) }, { "sheetProfileEntities" : qUnion([Q2]) }], "guidesArray" : [{ "guideEntities" : qUnion([Q3]), "guideDerivativeType" : LoftGuideDerivativeType.DEFAULT, "guideDerivativeMagnitude" : 1 }]});
        }
        {
            var Q0;
            Q0=qCreatedBy(makeId("Top.planeOp"),FACE);
            cPlane(context, id + "F58", {"entities" : qUnion([Q0]), "cplaneType" : CPlaneType.OFFSET, "offset" : 2000 * mm, "width" : 150 * mm, "height" : 150 * mm});
        }
        {
            var Q0;
            Q0=qCreatedBy(id+"F58.planeOp",FACE);
            var sketch = newSketch(context, id + "F59", { "sketchPlane" : qUnion([Q0])});
            skLineSegment(sketch, "E70", {"start": v(0, 0) * mm, "end": v(0, 4500) * mm});
            skLineSegment(sketch, "E71", {"start": v(0, 4500) * mm, "end": v(0, 7369.2) * mm});
            skLineSegment(sketch, "E72", {"start": v(0, 7369.2) * mm, "end": v(0, 5235.43) * mm});
            skLineSegment(sketch, "E73", {"start": v(0, 6302.31) * mm, "end": v(0, 5302.31) * mm});
            skLineSegment(sketch, "E74", {"start": v(0, 6302.31) * mm, "end": v(0, 7302.31) * mm});
            skLineSegment(sketch, "E75", {"start": v(0, 6302.31) * mm, "end": v(0, 6552.31) * mm});
            skLineSegment(sketch, "E76", {"start": v(0, 6302.31) * mm, "end": v(-1200, 6302.31) * mm});
            skLineSegment(sketch, "E77", {"start": v(0, 6302.31) * mm, "end": v(1200, 6302.31) * mm});
            skLineSegment(sketch, "E78", {"start": v(0, 6552.31) * mm, "end": v(-1700, 6552.31) * mm});
            skLineSegment(sketch, "E79", {"start": v(0, 6552.31) * mm, "end": v(1700, 6552.31) * mm});
            skLineSegment(sketch, "E80", {"start": v(0, 7302.31) * mm, "end": v(-2000, 7302.31) * mm});
            skLineSegment(sketch, "E81", {"start": v(0, 7302.31) * mm, "end": v(2000, 7302.31) * mm});
            skLineSegment(sketch, "E82", {"start": v(-2000, 7302.31) * mm, "end": v(-2000, 7052.31) * mm});
            skLineSegment(sketch, "E83", {"start": v(2000, 7302.31) * mm, "end": v(2000, 7052.31) * mm});
            skFitSpline(sketch, "E84", {"points": [v(0, 5302.31) * mm, v(-1200, 6302.31) * mm, v(-2000, 7052.31) * mm], "startDerivative": vector(0, 5513.6) * mm, "endDerivative": vector(-1974.16, 3290.27) * mm});
            skFitSpline(sketch, "E85", {"points": [v(0, 5302.31) * mm, v(1200, 6302.31) * mm, v(2000, 7052.31) * mm], "startDerivative": vector(0, 5513.6) * mm, "endDerivative": vector(1974.16, 3290.27) * mm});
            skFitSpline(sketch, "E86", {"points": [v(0, 6552.31) * mm, v(-2000, 7302.31) * mm], "startDerivative": vector(0, 2250) * mm, "endDerivative": vector(-900, 2250) * mm});
            skFitSpline(sketch, "E87", {"points": [v(0, 6552.31) * mm, v(2000, 7302.31) * mm], "startDerivative": vector(0, 2250) * mm, "endDerivative": vector(900, 2250) * mm});
            skSolve(sketch);
        }
        {
            var Q0;
            Q0=qCreatedBy(makeId("Right.planeOp"),FACE);
            var sketch = newSketch(context, id + "F60", { "sketchPlane" : qUnion([Q0])});
            skFitSpline(sketch, "E88", {"points": [v(5302.31, 2000) * mm, v(5927.31, 2050) * mm, v(6552.31, 2000) * mm], "startDerivative": vector(1250, 150) * mm, "endDerivative": vector(1250, -150) * mm});
            skFitSpline(sketch, "E89", {"points": [v(5302.31, 2000) * mm, v(5927.31, 1950) * mm, v(6552.31, 2000) * mm], "startDerivative": vector(1250, -150) * mm, "endDerivative": vector(1250, 150) * mm});
            skSolve(sketch);
        }
        {
            var Q0;
            Q0=qCreatedBy(makeId("Right.planeOp"),FACE);
            cPlane(context, id + "F61", {"entities" : qUnion([Q0]), "cplaneType" : CPlaneType.OFFSET, "offset" : 2000 * mm, "oppositeDirection" : true, "width" : 150 * mm, "height" : 150 * mm});
        }
        {
            var Q0;
            Q0=qCreatedBy(id+"F61.planeOp",FACE);
            var sketch = newSketch(context, id + "F62", { "sketchPlane" : qUnion([Q0])});
            skFitSpline(sketch, "E90", {"points": [v(7052.31, 2000) * mm, v(7177.31, 2010) * mm, v(7302.31, 2000) * mm], "startDerivative": vector(250, 30) * mm, "endDerivative": vector(250, -30) * mm});
            skFitSpline(sketch, "E91", {"points": [v(7052.31, 2000) * mm, v(7177.31, 1990) * mm, v(7302.31, 2000) * mm], "startDerivative": vector(250, -30) * mm, "endDerivative": vector(250, 30) * mm});
            skSolve(sketch);
        }
        {
            var Q0;
            Q0=qCreatedBy(makeId("Right.planeOp"),FACE);
            cPlane(context, id + "F63", {"entities" : qUnion([Q0]), "cplaneType" : CPlaneType.OFFSET, "offset" : 2000 * mm, "width" : 150 * mm, "height" : 150 * mm});
        }
        {
            var Q0;
            Q0=qCreatedBy(id+"F63.planeOp",FACE);
            var sketch = newSketch(context, id + "F64", { "sketchPlane" : qUnion([Q0])});
            skFitSpline(sketch, "E92", {"points": [v(7052.31, 2000) * mm, v(7177.31, 2010) * mm, v(7302.31, 2000) * mm], "startDerivative": vector(250, 30) * mm, "endDerivative": vector(250, -30) * mm});
            skFitSpline(sketch, "E93", {"points": [v(7052.31, 2000) * mm, v(7177.31, 1990) * mm, v(7302.31, 2000) * mm], "startDerivative": vector(250, -30) * mm, "endDerivative": vector(250, 30) * mm});
            skSolve(sketch);
        }
        {
            var Q1;
            Q1 = qSketchRegion(id + "F60", true);
            var Q2;
            Q2=makeQuery(id+"F62.imprint","IMPRINT",FACE,{"disambiguationData":[TD([[makeQuery(id+"F62.imprint","IMPRINT",EDGE,{"derivedFrom":sQuery(id+"F62.wireOp",EDGE,"E90")}),-1.0]])]});
            var Q3;
            Q3=sQuery(id+"F59.wireOp",EDGE,"E84");
            var Q4;
            Q4=sQuery(id+"F59.wireOp",EDGE,"E86");
            loft(context, id + "F65", {"addGuides" : true, "sheetProfilesArray" : [{ "sheetProfileEntities" : qUnion([Q1]) }, { "sheetProfileEntities" : qUnion([Q2]) }], "guidesArray" : [{ "guideEntities" : qUnion([Q3]), "guideDerivativeType" : LoftGuideDerivativeType.DEFAULT, "guideDerivativeMagnitude" : 1 }, { "guideEntities" : qUnion([Q4]), "guideDerivativeType" : LoftGuideDerivativeType.DEFAULT, "guideDerivativeMagnitude" : 1 }]});
        }
        {
            var Q1;
            Q1 = qSketchRegion(id + "F60", true);
            var Q2;
            Q2=makeQuery(id+"F64.imprint","IMPRINT",FACE,{"disambiguationData":[TD([[makeQuery(id+"F64.imprint","IMPRINT",EDGE,{"derivedFrom":sQuery(id+"F64.wireOp",EDGE,"E92")}),-1.0]])]});
            var Q3;
            Q3=sQuery(id+"F59.wireOp",EDGE,"E85");
            var Q4;
            Q4=sQuery(id+"F59.wireOp",EDGE,"E87");
            loft(context, id + "F66", {"operationType" : NewBodyOperationType.ADD, "addGuides" : true, "sheetProfilesArray" : [{ "sheetProfileEntities" : qUnion([Q1]) }, { "sheetProfileEntities" : qUnion([Q2]) }], "guidesArray" : [{ "guideEntities" : qUnion([Q3]), "guideDerivativeType" : LoftGuideDerivativeType.DEFAULT, "guideDerivativeMagnitude" : 1 }, { "guideEntities" : qUnion([Q4]), "guideDerivativeType" : LoftGuideDerivativeType.DEFAULT, "guideDerivativeMagnitude" : 1 }]});
        }
    });
